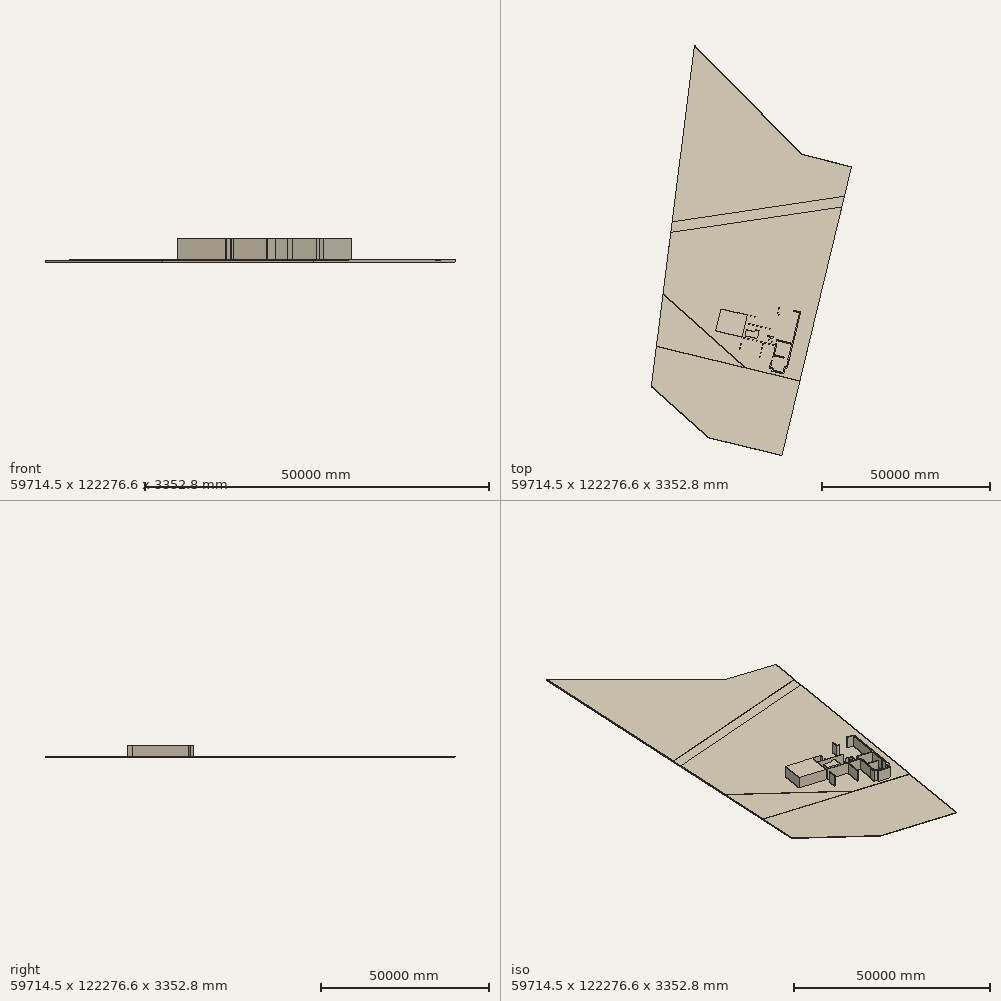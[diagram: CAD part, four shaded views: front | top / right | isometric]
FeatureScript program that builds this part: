
annotation { "Feature Type Name" : "Feature", "Feature Type Description" : "" }
export const myFeature = defineFeature(function(context is Context, id is Id, definition is map)
    precondition{}
    {
        {
            var Q0;
            Q0=qCreatedBy(makeId("Top.planeOp"),FACE);
            var sketch = newSketch(context, id + "F0", { "sketchPlane" : qUnion([Q0])});
            skLineSegment(sketch, "E0", {"start": v(0, 0) * mm, "end": v(31989.83, -32467.96) * mm});
            skLineSegment(sketch, "E1", {"start": v(31989.83, -32467.96) * mm, "end": v(46862.18, -36229.17) * mm});
            skLineSegment(sketch, "E2", {"start": v(46862.18, -36229.17) * mm, "end": v(26112.23, -122276.56) * mm});
            skLineSegment(sketch, "E3", {"start": v(46862.18, -36229.17) * mm, "end": v(46862.18, -51469.17) * mm, "construction": true});
            skLineSegment(sketch, "E4", {"start": v(0, 0) * mm, "end": v(-12852.3, -101676.89) * mm});
            skLineSegment(sketch, "E5", {"start": v(0, 0) * mm, "end": v(0, 15240) * mm, "construction": true});
            skLineSegment(sketch, "E6", {"start": v(26112.23, -122276.56) * mm, "end": v(4230, -116999.76) * mm});
            skLineSegment(sketch, "E7", {"start": v(26112.23, -122276.56) * mm, "end": v(10872.23, -122276.56) * mm, "construction": true});
            skLineSegment(sketch, "E8", {"start": v(4230, -116999.76) * mm, "end": v(-12852.3, -101676.89) * mm});
            skArc(sketch, "E9", {"start": v(-4165.07, -109469.35) * mm, "mid": v(-689.73, -114039.67) * mm, "end": v(4230, -116999.76) * mm, "construction": true});
            skArc(sketch, "E10", {"start": v(-4165.07, -109469.35) * mm, "mid": v(-8132.26, -105153.47) * mm, "end": v(-12852.3, -101676.89) * mm, "construction": true});
            skLineSegment(sketch, "E11", {"start": v(31471.2, -100053.58) * mm, "end": v(-11342.08, -89729.35) * mm});
            skLineSegment(sketch, "E12", {"start": v(-9365.85, -74095.03) * mm, "end": v(15198.72, -96129.54) * mm});
            skLineSegment(sketch, "E13", {"start": v(-6651.63, -52622.31) * mm, "end": v(44754.67, -44968.73) * mm});
            skLineSegment(sketch, "E14", {"start": v(-7048.63, -55763.02) * mm, "end": v(43983.88, -48165.09) * mm});
            skSolve(sketch);
        }
        {
            var Q0;
            {var subQ4=sQuery(id+"F0.wireOp",EDGE,"E0");Q0=makeQuery(id+"F0.imprint","IMPRINT",FACE,{"disambiguationData":[TD([[makeQuery(id+"F0.imprint","IMPRINT",EDGE,{"derivedFrom":subQ4}),-1.0]])]});}
            var Q1;
            {var subQ0=sQuery(id+"F0.wireOp",EDGE,"E13");Q1=makeQuery(id+"F0.imprint","IMPRINT",FACE,{"disambiguationData":[TD([[makeQuery(id+"F0.imprint","IMPRINT",EDGE,{"derivedFrom":subQ0}),-1.0]])]});}
            var Q2;
            {var subQ0=sQuery(id+"F0.wireOp",EDGE,"E12");Q2=makeQuery(id+"F0.imprint","IMPRINT",FACE,{"disambiguationData":[TD([[makeQuery(id+"F0.imprint","IMPRINT",EDGE,{"derivedFrom":subQ0}),1.0]])]});}
            var Q3;
            {var subQ3=sQuery(id+"F0.wireOp",EDGE,"E12");Q3=makeQuery(id+"F0.imprint","IMPRINT",FACE,{"disambiguationData":[TD([[makeQuery(id+"F0.imprint","IMPRINT",EDGE,{"derivedFrom":subQ3}),-1.0]])]});}
            var Q4;
            {var subQ1=sQuery(id+"F0.wireOp",EDGE,"E6");Q4=makeQuery(id+"F0.imprint","IMPRINT",FACE,{"disambiguationData":[TD([[makeQuery(id+"F0.imprint","IMPRINT",EDGE,{"derivedFrom":subQ1}),-1.0]])]});}
            extrude(context, id + "F1", {"entities" : qUnion([Q0, Q1, Q2, Q3, Q4]), "depth" : 304.8 * mm, "offsetDistance" : 25.4 * mm});
        }
        {
            var Q0;
            Q0=makeQuery(id+"F1.opExtrude","CAP_FACE",FACE,{"disambiguationData":[OSD([sQuery(id+"F0.wireOp",EDGE,"E0"),sQuery(id+"F0.wireOp",EDGE,"E1"),sQuery(id+"F0.wireOp",EDGE,"E2"),sQuery(id+"F0.wireOp",EDGE,"E4"),sQuery(id+"F0.wireOp",EDGE,"E6"),sQuery(id+"F0.wireOp",EDGE,"E8")])],"isStart":false});
            var sketch = newSketch(context, id + "F2", { "sketchPlane" : qUnion([Q0])});
            skLineSegment(sketch, "E15.0", {"start": v(-9365.85, -74095.03) * mm, "end": v(15198.72, -96129.54) * mm});
            skLineSegment(sketch, "E16.0", {"start": v(31471.2, -100053.58) * mm, "end": v(-11342.08, -89729.35) * mm});
            skLineSegment(sketch, "E17.0", {"start": v(0, 0) * mm, "end": v(-12852.3, -101676.89) * mm});
            skSolve(sketch);
        }
        {
            var Q0;
            {var subQ0=sQuery(id+"F2.wireOp",EDGE,"E15.0");Q0=makeQuery(id+"F2.imprint","IMPRINT",FACE,{"disambiguationData":[TD([[makeQuery(id+"F2.imprint","IMPRINT",EDGE,{"derivedFrom":subQ0}),-1.0]])]});}
            extrude(context, id + "F3", {"entities" : qUnion([Q0]), "operationType" : NewBodyOperationType.REMOVE, "oppositeDirection" : true, "depth" : 76.2 * mm, "offsetDistance" : 25.4 * mm});
        }
        {
            var Q0;
            Q0=makeQuery(id+"F1.opExtrude","CAP_FACE",FACE,{"disambiguationData":[OSD([sQuery(id+"F0.wireOp",EDGE,"E0"),sQuery(id+"F0.wireOp",EDGE,"E1"),sQuery(id+"F0.wireOp",EDGE,"E2"),sQuery(id+"F0.wireOp",EDGE,"E4"),sQuery(id+"F0.wireOp",EDGE,"E6"),sQuery(id+"F0.wireOp",EDGE,"E8")])],"isStart":false});
            var sketch = newSketch(context, id + "F4", { "sketchPlane" : qUnion([Q0])});
            skLineSegment(sketch, "E18.0", {"start": v(0, 0) * mm, "end": v(-12852.3, -101676.89) * mm});
            skLineSegment(sketch, "E19.0", {"start": v(4230, -116999.76) * mm, "end": v(-12852.3, -101676.89) * mm});
            skLineSegment(sketch, "E20.0", {"start": v(26112.23, -122276.56) * mm, "end": v(4230, -116999.76) * mm});
            skLineSegment(sketch, "E21.0", {"start": v(46862.18, -36229.17) * mm, "end": v(26112.23, -122276.56) * mm});
            skLineSegment(sketch, "E22.0", {"start": v(31471.2, -100053.58) * mm, "end": v(-11342.08, -89729.35) * mm});
            skSolve(sketch);
        }
        {
            var Q0;
            {var subQ4=sQuery(id+"F4.wireOp",EDGE,"E19.0");Q0=makeQuery(id+"F4.imprint","IMPRINT",FACE,{"disambiguationData":[TD([[makeQuery(id+"F4.imprint","IMPRINT",EDGE,{"derivedFrom":subQ4}),-1.0]])]});}
            extrude(context, id + "F5", {"entities" : qUnion([Q0]), "operationType" : NewBodyOperationType.REMOVE, "oppositeDirection" : true, "depth" : 152.4 * mm, "offsetDistance" : 25.4 * mm});
        }
        {
            var Q0;
            Q0=makeQuery(id+"F1.opExtrude","CAP_FACE",FACE,{"disambiguationData":[OSD([sQuery(id+"F0.wireOp",EDGE,"E0"),sQuery(id+"F0.wireOp",EDGE,"E1"),sQuery(id+"F0.wireOp",EDGE,"E2"),sQuery(id+"F0.wireOp",EDGE,"E4"),sQuery(id+"F0.wireOp",EDGE,"E6"),sQuery(id+"F0.wireOp",EDGE,"E8")])],"isStart":false});
            var sketch = newSketch(context, id + "F6", { "sketchPlane" : qUnion([Q0])});
            skLineSegment(sketch, "E23.0", {"start": v(-6651.63, -52622.31) * mm, "end": v(44754.67, -44968.73) * mm});
            skLineSegment(sketch, "E24.0", {"start": v(-7048.63, -55763.02) * mm, "end": v(43983.88, -48165.09) * mm});
            skLineSegment(sketch, "E25.0", {"start": v(0, 0) * mm, "end": v(-12852.3, -101676.89) * mm});
            skLineSegment(sketch, "E26.0", {"start": v(46862.18, -36229.17) * mm, "end": v(26112.23, -122276.56) * mm});
            skSolve(sketch);
        }
        {
            var Q0;
            {var subQ0=sQuery(id+"F6.wireOp",EDGE,"E23.0");Q0=makeQuery(id+"F6.imprint","IMPRINT",FACE,{"disambiguationData":[TD([[makeQuery(id+"F6.imprint","IMPRINT",EDGE,{"derivedFrom":subQ0}),-1.0]])]});}
            extrude(context, id + "F7", {"entities" : qUnion([Q0]), "operationType" : NewBodyOperationType.REMOVE, "oppositeDirection" : true, "depth" : 152.4 * mm, "offsetDistance" : 25.4 * mm});
        }
        {
            var Q0;
            {var subQ0=sQuery(id+"F0.wireOp",EDGE,"E4");var subQ1=sQuery(id+"F0.wireOp",EDGE,"E2");Q0=makeQuery(id+"F7.boolean.opBoolean","SPLIT",FACE,{"disambiguationData":[TD([makeQuery(id+"F3.boolean.opBoolean","COPY",FACE,{"derivedFrom":makeQuery(id+"F3.opExtrude","SWEPT_FACE",FACE,{"disambiguationData":[OSD([sQuery(id+"F2.wireOp",EDGE,"E15.0")])]})})])],"derivedFrom":makeQuery(id+"F1.opExtrude","CAP_FACE",FACE,{"disambiguationData":[OSD([sQuery(id+"F0.wireOp",EDGE,"E0"),sQuery(id+"F0.wireOp",EDGE,"E1"),subQ1,subQ0,sQuery(id+"F0.wireOp",EDGE,"E6"),sQuery(id+"F0.wireOp",EDGE,"E8")])],"isStart":false})});}
            var sketch = newSketch(context, id + "F8", { "sketchPlane" : qUnion([Q0])});
            skLineSegment(sketch, "E27", {"start": v(27669.68, -96315.03) * mm, "end": v(31724.64, -79499.64) * mm});
            skPoint(sketch, "E28.orphan", {"position": v(31471.2, -100053.58) * mm});
            skLineSegment(sketch, "E29", {"start": v(-5717.12, -79311.3) * mm, "end": v(3764.68, -81597.8) * mm});
            skLineSegment(sketch, "E30", {"start": v(3764.68, -81597.8) * mm, "end": v(7766.05, -65004.64) * mm});
            skLineSegment(sketch, "E31", {"start": v(7766.05, -65004.64) * mm, "end": v(-1715.76, -62718.14) * mm});
            skLineSegment(sketch, "E32", {"start": v(-1715.76, -62718.14) * mm, "end": v(-5717.12, -79311.3) * mm});
            skLineSegment(sketch, "E33", {"start": v(-5145.5, -76940.85) * mm, "end": v(-2182.44, -77655.38) * mm});
            skLineSegment(sketch, "E34", {"start": v(-2182.44, -77655.38) * mm, "end": v(-2754.06, -80025.83) * mm});
            skLineSegment(sketch, "E35", {"start": v(-5145.5, -76940.85) * mm, "end": v(-9590.1, -75869.05) * mm});
            skLineSegment(sketch, "E36", {"start": v(-2182.44, -77655.38) * mm, "end": v(1247.3, -63432.67) * mm});
            skLineSegment(sketch, "E37", {"start": v(3764.68, -81597.8) * mm, "end": v(7190.64, -82423.95) * mm});
            skLineSegment(sketch, "E38", {"start": v(4934.3, -91780.7) * mm, "end": v(-10343.91, -88096.42) * mm});
            skLineSegment(sketch, "E39.0", {"start": v(4230, -116999.76) * mm, "end": v(-12852.3, -101676.89) * mm});
            skLineSegment(sketch, "E40", {"start": v(-2047.33, -90097.1) * mm, "end": v(-6264.7, -107585.98) * mm});
            skLineSegment(sketch, "E41", {"start": v(-5603, -89239.67) * mm, "end": v(-9358.03, -104811.25) * mm});
            skArc(sketch, "E42", {"start": v(-6746.26, -93980.57) * mm, "mid": v(-7326.44, -90293.4) * mm, "end": v(-10343.91, -88096.42) * mm});
            skLineSegment(sketch, "E43", {"start": v(-8087.58, -78739.68) * mm, "end": v(-10343.91, -88096.42) * mm});
            skLineSegment(sketch, "E44", {"start": v(-5717.12, -79311.3) * mm, "end": v(-8087.58, -78739.68) * mm});
            skLineSegment(sketch, "E45", {"start": v(22775.38, -94507.71) * mm, "end": v(22346.66, -96285.55) * mm});
            skLineSegment(sketch, "E46", {"start": v(22346.66, -96285.55) * mm, "end": v(23235.58, -96499.91) * mm});
            skLineSegment(sketch, "E47", {"start": v(23235.58, -96499.91) * mm, "end": v(23092.67, -97092.52) * mm});
            skLineSegment(sketch, "E48", {"start": v(23092.67, -97092.52) * mm, "end": v(26648.35, -97949.96) * mm});
            skLineSegment(sketch, "E49", {"start": v(26648.35, -97949.96) * mm, "end": v(27077.07, -96172.12) * mm});
            skLineSegment(sketch, "E50", {"start": v(13071.34, -92167.63) * mm, "end": v(14241.39, -87315.61) * mm});
            skLineSegment(sketch, "E51", {"start": v(14241.39, -87315.61) * mm, "end": v(5985.04, -85324.63) * mm});
            skLineSegment(sketch, "E52", {"start": v(5985.04, -85324.63) * mm, "end": v(7699.91, -78213.28) * mm});
            skLineSegment(sketch, "E53", {"start": v(14020.33, -75230.32) * mm, "end": v(31724.64, -79499.64) * mm});
            skLineSegment(sketch, "E54.trimOffspring", {"start": v(27077.07, -96172.12) * mm, "end": v(27669.68, -96315.03) * mm});
            skLineSegment(sketch, "E55.0", {"start": v(6352.8, -85099.78) * mm, "end": v(7924.77, -78581.03) * mm});
            skLineSegment(sketch, "E55.1", {"start": v(23460.43, -96867.67) * mm, "end": v(26423.5, -97582.2) * mm});
            skLineSegment(sketch, "E55.2", {"start": v(26423.5, -97582.2) * mm, "end": v(26852.22, -95804.36) * mm});
            skLineSegment(sketch, "E55.3", {"start": v(26852.22, -95804.36) * mm, "end": v(27444.83, -95947.27) * mm});
            skLineSegment(sketch, "E55.4", {"start": v(27444.83, -95947.27) * mm, "end": v(28016.45, -93576.82) * mm});
            skLineSegment(sketch, "E55.5", {"start": v(23603.34, -96275.06) * mm, "end": v(23460.43, -96867.67) * mm});
            skLineSegment(sketch, "E55.6", {"start": v(14245.18, -75598.08) * mm, "end": v(19282.4, -76812.78) * mm});
            skLineSegment(sketch, "E55.7", {"start": v(22714.42, -96060.7) * mm, "end": v(23603.34, -96275.06) * mm});
            skLineSegment(sketch, "E55.8", {"start": v(23143.14, -94282.86) * mm, "end": v(22714.42, -96060.7) * mm});
            skLineSegment(sketch, "E55.9", {"start": v(13439.1, -91942.77) * mm, "end": v(23143.14, -94282.86) * mm});
            skLineSegment(sketch, "E55.10", {"start": v(13439.1, -91942.77) * mm, "end": v(14609.14, -87090.76) * mm});
            skLineSegment(sketch, "E55.11", {"start": v(14609.14, -87090.76) * mm, "end": v(6352.8, -85099.78) * mm});
            skLineSegment(sketch, "E56", {"start": v(14609.14, -87090.76) * mm, "end": v(19350.05, -88234) * mm});
            skLineSegment(sketch, "E57", {"start": v(20619.6, -88657.73) * mm, "end": v(19476.35, -93398.63) * mm});
            skLineSegment(sketch, "E58.0", {"start": v(20508.48, -88630.93) * mm, "end": v(19365.23, -93371.83) * mm});
            skLineSegment(sketch, "E58.1", {"start": v(14582.35, -87201.87) * mm, "end": v(20508.48, -88630.93) * mm});
            skLineSegment(sketch, "E59", {"start": v(17710.43, -83331.52) * mm, "end": v(18255.26, -81072.19) * mm});
            skLineSegment(sketch, "E60", {"start": v(17821.54, -83358.32) * mm, "end": v(18393.17, -80987.87) * mm});
            skLineSegment(sketch, "E61", {"start": v(7924.77, -78581.03) * mm, "end": v(18255.26, -81072.19) * mm});
            skLineSegment(sketch, "E62", {"start": v(14020.33, -75230.32) * mm, "end": v(12993.2, -79489.73) * mm});
            skLineSegment(sketch, "E63", {"start": v(12993.2, -79489.73) * mm, "end": v(7699.91, -78213.28) * mm});
            skLineSegment(sketch, "E64", {"start": v(14245.18, -75598.08) * mm, "end": v(13218.05, -79857.49) * mm});
            skLineSegment(sketch, "E65", {"start": v(13244.84, -79746.37) * mm, "end": v(18985.78, -81130.77) * mm});
            skLineSegment(sketch, "E66", {"start": v(23143.14, -94282.86) * mm, "end": v(23571.86, -92505.02) * mm});
            skLineSegment(sketch, "E67", {"start": v(24202.07, -89404.05) * mm, "end": v(19350.05, -88234) * mm});
            skLineSegment(sketch, "E68", {"start": v(23032.02, -94256.07) * mm, "end": v(24175.27, -89515.16) * mm});
            skLineSegment(sketch, "E69", {"start": v(24175.27, -89515.16) * mm, "end": v(20619.6, -88657.73) * mm});
            skLineSegment(sketch, "E70", {"start": v(19833.61, -91917.1) * mm, "end": v(21018.84, -92202.9) * mm});
            skLineSegment(sketch, "E71", {"start": v(21018.84, -92202.9) * mm, "end": v(21519, -90128.76) * mm});
            skLineSegment(sketch, "E72", {"start": v(21519, -90128.76) * mm, "end": v(23889.46, -90700.39) * mm});
            skLineSegment(sketch, "E73", {"start": v(23571.86, -92505.02) * mm, "end": v(28016.45, -93576.82) * mm});
            skLineSegment(sketch, "E74", {"start": v(23828.5, -92253.37) * mm, "end": v(27982.96, -93255.2) * mm});
            skLineSegment(sketch, "E75", {"start": v(28983.3, -89106.91) * mm, "end": v(24828.84, -88105.08) * mm});
            skLineSegment(sketch, "E76", {"start": v(27982.96, -93255.2) * mm, "end": v(28983.3, -89106.91) * mm});
            skLineSegment(sketch, "E77", {"start": v(23828.5, -92253.37) * mm, "end": v(24828.84, -88105.08) * mm});
            skLineSegment(sketch, "E78.trimOffspring", {"start": v(29159.7, -88835.91) * mm, "end": v(31356.88, -79724.5) * mm});
            skLineSegment(sketch, "E79", {"start": v(29159.7, -88835.91) * mm, "end": v(24603.99, -87737.32) * mm});
            skLineSegment(sketch, "E80", {"start": v(24603.99, -87737.32) * mm, "end": v(24202.07, -89404.05) * mm});
            skLineSegment(sketch, "E81", {"start": v(26023.36, -78438.34) * mm, "end": v(24951.57, -82882.93) * mm});
            skLineSegment(sketch, "E82", {"start": v(24951.57, -82882.93) * mm, "end": v(30285.09, -84169.09) * mm});
            skLineSegment(sketch, "E83", {"start": v(25912.25, -78411.54) * mm, "end": v(24340.28, -84930.28) * mm});
            skLineSegment(sketch, "E84", {"start": v(24924.77, -82994.05) * mm, "end": v(30258.3, -84280.2) * mm});
            skLineSegment(sketch, "E85", {"start": v(21057.5, -78390.48) * mm, "end": v(23724.26, -79033.55) * mm});
            skLineSegment(sketch, "E86", {"start": v(23724.26, -79033.55) * mm, "end": v(23474.18, -80070.63) * mm});
            skLineSegment(sketch, "E87", {"start": v(23474.18, -80070.63) * mm, "end": v(20807.42, -79427.55) * mm});
            skLineSegment(sketch, "E88", {"start": v(20807.42, -79427.55) * mm, "end": v(21057.5, -78390.48) * mm});
            skLineSegment(sketch, "E89", {"start": v(12993.2, -79489.73) * mm, "end": v(12921.74, -79786.03) * mm});
            skLineSegment(sketch, "E90", {"start": v(17821.54, -83358.32) * mm, "end": v(24340.28, -84930.28) * mm});
            skLineSegment(sketch, "E91", {"start": v(25961.85, -83244.13) * mm, "end": v(25553.97, -84935.55) * mm});
            skLineSegment(sketch, "E92", {"start": v(15313.18, -82871.01) * mm, "end": v(24424.6, -85068.2) * mm});
            skLineSegment(sketch, "E93", {"start": v(24424.6, -85068.2) * mm, "end": v(24924.77, -82994.05) * mm});
            skLineSegment(sketch, "E94", {"start": v(25054.81, -81967.22) * mm, "end": v(24462.2, -81824.31) * mm});
            skLineSegment(sketch, "E95", {"start": v(24462.2, -81824.31) * mm, "end": v(23747.67, -84787.38) * mm});
            skLineSegment(sketch, "E96", {"start": v(22853.5, -83944.68) * mm, "end": v(17964.45, -82765.7) * mm});
            skLineSegment(sketch, "E97", {"start": v(18807.15, -81871.54) * mm, "end": v(19343.04, -79649.24) * mm});
            skLineSegment(sketch, "E98", {"start": v(20165.76, -80788.24) * mm, "end": v(19879.94, -81973.47) * mm});
            skLineSegment(sketch, "E99", {"start": v(19879.94, -81973.47) * mm, "end": v(23139.32, -82759.45) * mm});
            skLineSegment(sketch, "E100", {"start": v(23139.32, -82759.45) * mm, "end": v(23425.13, -81574.23) * mm});
            skLineSegment(sketch, "E101", {"start": v(23425.13, -81574.23) * mm, "end": v(20165.76, -80788.24) * mm});
            skLineSegment(sketch, "E102", {"start": v(19282.4, -76812.78) * mm, "end": v(25912.25, -78411.54) * mm});
            skLineSegment(sketch, "E103.trimOffspring", {"start": v(26023.36, -78438.34) * mm, "end": v(31356.88, -79724.5) * mm});
            skLineSegment(sketch, "E104", {"start": v(27837.43, -93533.65) * mm, "end": v(27908.89, -93237.34) * mm});
            skLineSegment(sketch, "E105", {"start": v(26948.51, -93319.29) * mm, "end": v(27019.97, -93022.98) * mm});
            skLineSegment(sketch, "E106", {"start": v(26972.33, -93220.52) * mm, "end": v(27861.25, -93434.88) * mm});
            skLineSegment(sketch, "E107", {"start": v(26963.4, -93257.56) * mm, "end": v(27852.32, -93471.92) * mm});
            skLineSegment(sketch, "E108", {"start": v(24810.98, -88179.16) * mm, "end": v(24514.67, -88107.7) * mm});
            skLineSegment(sketch, "E109", {"start": v(24300.31, -88996.63) * mm, "end": v(24596.62, -89068.08) * mm});
            skLineSegment(sketch, "E110", {"start": v(24362.04, -89011.51) * mm, "end": v(24576.4, -88122.6) * mm});
            skLineSegment(sketch, "E111", {"start": v(24399.08, -89020.44) * mm, "end": v(24613.44, -88131.52) * mm});
            skLineSegment(sketch, "E112", {"start": v(23016.84, -89118.24) * mm, "end": v(23543.8, -86932.98) * mm});
            skLineSegment(sketch, "E113", {"start": v(22905.73, -89091.44) * mm, "end": v(23405.9, -87017.3) * mm});
            skLineSegment(sketch, "E114", {"start": v(15884.8, -80500.56) * mm, "end": v(14312.84, -87019.3) * mm});
            skLineSegment(sketch, "E115", {"start": v(15339.97, -82759.9) * mm, "end": v(17710.43, -83331.52) * mm});
            skLineSegment(sketch, "E116", {"start": v(18807.15, -81871.54) * mm, "end": v(18214.53, -81728.63) * mm});
            skLineSegment(sketch, "E117", {"start": v(13071.34, -92167.63) * mm, "end": v(23071.68, -94579.17) * mm});
            skLineSegment(sketch, "E118", {"start": v(19247.36, -85896.9) * mm, "end": v(23543.8, -86932.98) * mm});
            skLineSegment(sketch, "E119", {"start": v(19109.45, -85981.23) * mm, "end": v(19739.1, -86133.06) * mm});
            skLineSegment(sketch, "E120", {"start": v(22016.8, -88877.08) * mm, "end": v(22516.98, -86802.94) * mm});
            skLineSegment(sketch, "E121", {"start": v(21905.7, -88850.29) * mm, "end": v(22405.86, -86776.14) * mm});
            skLineSegment(sketch, "E122", {"start": v(20090.81, -88412.64) * mm, "end": v(20590.98, -86338.5) * mm});
            skLineSegment(sketch, "E123", {"start": v(20201.93, -88439.43) * mm, "end": v(20702.1, -86365.29) * mm});
            skLineSegment(sketch, "E124", {"start": v(20344.83, -87846.82) * mm, "end": v(22048.6, -88257.67) * mm});
            skCircle(sketch, "E125", {"center": v(20717.84, -88250.3) * mm, "radius": 152.4 * mm});
            skCircle(sketch, "E126", {"center": v(21532.68, -88446.8) * mm, "radius": 152.4 * mm});
            skLineSegment(sketch, "E127", {"start": v(19473.5, -88263.78) * mm, "end": v(19544.96, -87967.47) * mm});
            skLineSegment(sketch, "E128", {"start": v(19544.96, -87967.47) * mm, "end": v(20038.8, -88086.56) * mm});
            skLineSegment(sketch, "E129", {"start": v(20038.8, -88086.56) * mm, "end": v(19967.35, -88382.87) * mm});
            skLineSegment(sketch, "E130", {"start": v(19643.73, -87991.29) * mm, "end": v(19756.86, -87522.14) * mm});
            skLineSegment(sketch, "E131", {"start": v(19756.86, -87522.14) * mm, "end": v(20053.17, -87593.59) * mm});
            skLineSegment(sketch, "E132", {"start": v(20053.17, -87593.59) * mm, "end": v(19940.04, -88062.74) * mm});
            skLineSegment(sketch, "E133", {"start": v(19760.9, -86530.24) * mm, "end": v(20501.67, -86708.88) * mm});
            skLineSegment(sketch, "E134", {"start": v(20600.87, -86785.05) * mm, "end": v(20489.76, -86758.26) * mm});
            skLineSegment(sketch, "E135", {"start": v(20346.85, -87350.87) * mm, "end": v(20457.97, -87377.67) * mm});
            skLineSegment(sketch, "E136", {"start": v(20402.41, -87364.27) * mm, "end": v(20545.32, -86771.66) * mm});
            skArc(sketch, "E137", {"start": v(20402.41, -87364.27) * mm, "mid": v(20012.42, -87067.68) * mm, "end": v(19966.67, -86579.86) * mm, "construction": true});
            skLineSegment(sketch, "E138", {"start": v(22231.16, -87988.16) * mm, "end": v(23120.08, -88202.52) * mm});
            skLineSegment(sketch, "E139", {"start": v(23120.08, -88202.52) * mm, "end": v(22016.8, -88877.08) * mm});
            skLineSegment(sketch, "E140", {"start": v(22231.16, -87988.16) * mm, "end": v(22905.73, -89091.44) * mm});
            skCircle(sketch, "E141", {"center": v(22568.44, -88539.8) * mm, "radius": 50.8 * mm});
            skLineSegment(sketch, "E142", {"start": v(22427.66, -87173.32) * mm, "end": v(23316.58, -87387.68) * mm});
            skLineSegment(sketch, "E143", {"start": v(22304.64, -87195.9) * mm, "end": v(22415.75, -87222.7) * mm});
            skLineSegment(sketch, "E144", {"start": v(22161.73, -87788.52) * mm, "end": v(22272.85, -87815.32) * mm});
            skLineSegment(sketch, "E145", {"start": v(22360.2, -87209.3) * mm, "end": v(22217.29, -87801.92) * mm});
            skArc(sketch, "E146", {"start": v(22217.29, -87801.92) * mm, "mid": v(22699.6, -87715.68) * mm, "end": v(22962.65, -87302.33) * mm, "construction": true});
            skLineSegment(sketch, "E147", {"start": v(19461.72, -85007.99) * mm, "end": v(21239.56, -85436.7) * mm});
            skLineSegment(sketch, "E148", {"start": v(19390.27, -85304.3) * mm, "end": v(21168.1, -85733.01) * mm});
            skLineSegment(sketch, "E149", {"start": v(20612.78, -86735.67) * mm, "end": v(20909.09, -86807.12) * mm});
            skLineSegment(sketch, "E150", {"start": v(21239.56, -85436.7) * mm, "end": v(21025.2, -86325.63) * mm});
            skLineSegment(sketch, "E151", {"start": v(21980.33, -85615.34) * mm, "end": v(21765.97, -86504.26) * mm});
            skLineSegment(sketch, "E152", {"start": v(21099.28, -86343.49) * mm, "end": v(21072.48, -86454.6) * mm});
            skLineSegment(sketch, "E153", {"start": v(21691.9, -86486.4) * mm, "end": v(21665.1, -86597.5) * mm});
            skLineSegment(sketch, "E154", {"start": v(21085.88, -86399.05) * mm, "end": v(21678.5, -86541.95) * mm});
            skLineSegment(sketch, "E155", {"start": v(20909.09, -86807.12) * mm, "end": v(20998.4, -86436.74) * mm});
            skLineSegment(sketch, "E156", {"start": v(21649.86, -86985.76) * mm, "end": v(21739.17, -86615.37) * mm});
            skLineSegment(sketch, "E157.trimOffspring", {"start": v(21649.86, -86985.76) * mm, "end": v(22316.55, -87146.52) * mm});
            skLineSegment(sketch, "E158.trimOffspring", {"start": v(21908.87, -85911.64) * mm, "end": v(23686.71, -86340.36) * mm});
            skLineSegment(sketch, "E159.trimOffspring", {"start": v(21980.33, -85615.34) * mm, "end": v(23758.16, -86044.06) * mm});
            skLineSegment(sketch, "E160", {"start": v(15482.88, -82167.29) * mm, "end": v(17853.33, -82738.9) * mm});
            skLineSegment(sketch, "E161", {"start": v(15741.9, -81093.17) * mm, "end": v(18112.35, -81664.8) * mm});
            skLineSegment(sketch, "E162", {"start": v(17889.06, -82590.76) * mm, "end": v(18000.17, -82617.55) * mm});
            skLineSegment(sketch, "E163", {"start": v(18067.7, -81850) * mm, "end": v(18178.8, -81876.79) * mm});
            skLineSegment(sketch, "E164", {"start": v(18123.25, -81863.39) * mm, "end": v(17944.62, -82604.15) * mm});
            skLineSegment(sketch, "E165", {"start": v(15397.07, -82035.55) * mm, "end": v(15508.19, -82062.34) * mm});
            skLineSegment(sketch, "E166", {"start": v(15611.43, -81146.63) * mm, "end": v(15722.55, -81173.42) * mm});
            skLineSegment(sketch, "E167", {"start": v(15666.99, -81160.03) * mm, "end": v(15452.63, -82048.95) * mm});
            skLineSegment(sketch, "E168", {"start": v(22853.5, -83944.68) * mm, "end": v(22710.6, -84537.3) * mm});
            skLineSegment(sketch, "E169", {"start": v(22784.67, -84555.16) * mm, "end": v(22757.88, -84666.27) * mm});
            skLineSegment(sketch, "E170", {"start": v(23673.6, -84769.51) * mm, "end": v(23646.8, -84880.63) * mm});
            skLineSegment(sketch, "E171", {"start": v(25412.08, -80485.69) * mm, "end": v(24708.35, -80315.99) * mm});
            skLineSegment(sketch, "E172", {"start": v(24708.35, -80315.99) * mm, "end": v(25208.52, -78241.84) * mm});
            skLineSegment(sketch, "E173", {"start": v(25319.64, -78268.64) * mm, "end": v(24846.26, -80231.67) * mm});
            skLineSegment(sketch, "E174", {"start": v(24846.26, -80231.67) * mm, "end": v(25438.87, -80374.57) * mm});
            skLineSegment(sketch, "E175", {"start": v(26072.96, -83270.93) * mm, "end": v(25665.08, -84962.34) * mm});
            skLineSegment(sketch, "E176", {"start": v(25715.7, -84752.46) * mm, "end": v(29901.03, -85761.73) * mm});
            skLineSegment(sketch, "E177", {"start": v(25688.9, -84863.58) * mm, "end": v(29874.23, -85872.85) * mm});
            skLineSegment(sketch, "E178", {"start": v(28554.53, -83869.35) * mm, "end": v(28197.26, -85350.88) * mm});
            skLineSegment(sketch, "E179", {"start": v(28443.41, -83842.55) * mm, "end": v(28086.15, -85324.08) * mm});
            skLineSegment(sketch, "E180", {"start": v(27702.65, -83663.92) * mm, "end": v(27345.38, -85145.45) * mm});
            skLineSegment(sketch, "E181", {"start": v(25941.96, -83814.16) * mm, "end": v(26830.88, -84028.52) * mm});
            skLineSegment(sketch, "E182", {"start": v(26830.88, -84028.52) * mm, "end": v(26961.88, -83485.29) * mm});
            skLineSegment(sketch, "E183", {"start": v(27085.34, -83515.06) * mm, "end": v(27013.89, -83811.37) * mm});
            skLineSegment(sketch, "E184", {"start": v(27013.89, -83811.37) * mm, "end": v(27507.73, -83930.45) * mm});
            skLineSegment(sketch, "E185", {"start": v(27507.73, -83930.45) * mm, "end": v(27579.19, -83634.15) * mm});
            skLineSegment(sketch, "E186", {"start": v(27112.66, -83835.18) * mm, "end": v(26999.52, -84304.34) * mm});
            skLineSegment(sketch, "E187", {"start": v(26999.52, -84304.34) * mm, "end": v(27295.83, -84375.79) * mm});
            skLineSegment(sketch, "E188", {"start": v(27295.83, -84375.79) * mm, "end": v(27408.96, -83906.64) * mm});
            skLineSegment(sketch, "E189", {"start": v(25762.98, -84881.44) * mm, "end": v(25789.77, -84770.32) * mm});
            skLineSegment(sketch, "E190", {"start": v(26355.6, -85024.34) * mm, "end": v(26382.39, -84913.23) * mm});
            skLineSegment(sketch, "E191", {"start": v(25776.38, -84825.88) * mm, "end": v(26368.99, -84968.79) * mm});
            skArc(sketch, "E192", {"start": v(26368.99, -84968.79) * mm, "mid": v(26275.53, -84475.95) * mm, "end": v(25844.08, -84220.05) * mm, "construction": true});
            skLineSegment(sketch, "E193", {"start": v(28340.17, -84758.27) * mm, "end": v(30043.93, -85169.12) * mm});
            skLineSegment(sketch, "E194", {"start": v(28366.96, -84647.15) * mm, "end": v(30070.73, -85058) * mm});
            skLineSegment(sketch, "E195", {"start": v(29278.79, -88342.07) * mm, "end": v(27303.41, -87865.72) * mm});
            skLineSegment(sketch, "E196", {"start": v(27303.41, -87865.72) * mm, "end": v(27755.95, -85989.1) * mm});
            skLineSegment(sketch, "E197", {"start": v(27755.95, -85989.1) * mm, "end": v(29731.32, -86465.46) * mm});
            skLineSegment(sketch, "E198", {"start": v(28296.03, -85374.7) * mm, "end": v(28269.24, -85485.81) * mm});
            skLineSegment(sketch, "E199", {"start": v(29777.56, -85731.96) * mm, "end": v(29750.77, -85843.08) * mm});
            skLineSegment(sketch, "E200", {"start": v(29036.8, -85553.33) * mm, "end": v(29010, -85664.44) * mm});
            skLineSegment(sketch, "E201", {"start": v(28282.63, -85430.25) * mm, "end": v(29023.4, -85608.89) * mm});
            skLineSegment(sketch, "E202", {"start": v(29023.4, -85608.89) * mm, "end": v(29764.17, -85787.52) * mm});
            skArc(sketch, "E203", {"start": v(25137.16, -86664) * mm, "mid": v(24733.67, -87037.01) * mm, "end": v(24922.8, -87552.92) * mm});
            skLineSegment(sketch, "E204", {"start": v(26429.67, -85042.2) * mm, "end": v(26197.45, -86005.2) * mm});
            skLineSegment(sketch, "E205", {"start": v(26197.45, -86005.2) * mm, "end": v(25456.68, -85826.57) * mm});
            skLineSegment(sketch, "E206", {"start": v(26540.78, -85069) * mm, "end": v(26281.77, -86143.11) * mm});
            skLineSegment(sketch, "E207", {"start": v(26281.77, -86143.11) * mm, "end": v(25429.88, -85937.69) * mm});
            skLineSegment(sketch, "E208", {"start": v(26405.85, -85140.98) * mm, "end": v(26516.97, -85167.77) * mm});
            skLineSegment(sketch, "E209", {"start": v(26215.3, -85931.13) * mm, "end": v(26326.42, -85957.92) * mm});
            skLineSegment(sketch, "E210", {"start": v(26461.4, -85154.37) * mm, "end": v(26270.87, -85944.52) * mm});
            skArc(sketch, "E211", {"start": v(26270.87, -85944.52) * mm, "mid": v(26927.99, -85819.92) * mm, "end": v(27269.18, -85244.65) * mm, "construction": true});
            skLineSegment(sketch, "E212", {"start": v(25363.43, -85725.7) * mm, "end": v(25474.54, -85752.5) * mm});
            skLineSegment(sketch, "E213", {"start": v(25553.97, -84935.55) * mm, "end": v(25665.08, -84962.34) * mm});
            skLineSegment(sketch, "E214.trimOffspring", {"start": v(25363.43, -85725.7) * mm, "end": v(24863.26, -87799.85) * mm});
            skLineSegment(sketch, "E215.trimOffspring", {"start": v(25474.54, -85752.5) * mm, "end": v(24974.37, -87826.64) * mm});
            skLineSegment(sketch, "E216", {"start": v(24733.67, -87037.01) * mm, "end": v(25029.98, -87108.46) * mm, "construction": true});
            skLineSegment(sketch, "E217", {"start": v(23543.8, -86932.98) * mm, "end": v(23758.16, -86044.06) * mm});
            skLineSegment(sketch, "E218", {"start": v(20717.84, -88250.3) * mm, "end": v(21532.68, -88446.8) * mm, "construction": true});
            skLineSegment(sketch, "E219", {"start": v(14201.72, -86992.5) * mm, "end": v(15773.69, -80473.77) * mm});
            skLineSegment(sketch, "E220", {"start": v(15063.1, -83908.09) * mm, "end": v(19470.65, -84970.95) * mm});
            skLineSegment(sketch, "E221", {"start": v(19739.1, -86133.06) * mm, "end": v(19238.93, -88207.2) * mm});
            skLineSegment(sketch, "E222", {"start": v(19470.65, -84970.95) * mm, "end": v(19247.36, -85896.9) * mm});
            skLineSegment(sketch, "E223.trimOffspring", {"start": v(19850.22, -86159.86) * mm, "end": v(19350.05, -88234) * mm});
            skLineSegment(sketch, "E224.trimOffspring", {"start": v(19850.22, -86159.86) * mm, "end": v(23405.9, -87017.3) * mm});
            skLineSegment(sketch, "E225", {"start": v(15036.3, -84019.2) * mm, "end": v(19332.74, -85055.27) * mm});
            skLineSegment(sketch, "E226", {"start": v(19332.74, -85055.27) * mm, "end": v(19109.45, -85981.23) * mm});
            skLineSegment(sketch, "E227", {"start": v(23000.54, -90486.03) * mm, "end": v(23286.35, -89300.8) * mm});
            skLineSegment(sketch, "E228", {"start": v(20809.72, -93720.17) * mm, "end": v(20738.27, -94016.47) * mm});
            skLineSegment(sketch, "E229", {"start": v(21698.64, -93934.53) * mm, "end": v(21627.2, -94230.83) * mm});
            skLineSegment(sketch, "E230", {"start": v(20774, -93868.32) * mm, "end": v(21662.92, -94082.68) * mm});
            skLineSegment(sketch, "E231", {"start": v(18295.67, -84805.18) * mm, "end": v(18152.76, -85397.8) * mm});
            skLineSegment(sketch, "E232", {"start": v(18152.76, -85397.8) * mm, "end": v(15486, -84754.72) * mm});
            skLineSegment(sketch, "E233", {"start": v(15486, -84754.72) * mm, "end": v(15048.36, -86569.6) * mm});
            skLineSegment(sketch, "E234", {"start": v(15048.36, -86569.6) * mm, "end": v(18789.23, -87471.7) * mm});
            skLineSegment(sketch, "E235", {"start": v(18789.23, -87471.7) * mm, "end": v(19146.5, -85990.16) * mm});
            skLineSegment(sketch, "E236", {"start": v(18396.54, -84711.93) * mm, "end": v(18369.75, -84823.05) * mm});
            skLineSegment(sketch, "E237", {"start": v(19285.46, -84926.3) * mm, "end": v(19258.67, -85037.4) * mm});
            skLineSegment(sketch, "E238", {"start": v(18383.14, -84767.49) * mm, "end": v(19272.06, -84981.85) * mm});
            skArc(sketch, "E239", {"start": v(18383.14, -84767.49) * mm, "mid": v(18512.5, -85490.95) * mm, "end": v(19132.53, -85885.54) * mm, "construction": true});
            skArc(sketch, "E240", {"start": v(24399.08, -89020.44) * mm, "mid": v(25122.55, -88891.09) * mm, "end": v(25517.13, -88271.06) * mm, "construction": true});
            skArc(sketch, "E241", {"start": v(26972.33, -93220.52) * mm, "mid": v(27417.21, -92635.53) * mm, "end": v(28148.94, -92566.91) * mm, "construction": true});
            skArc(sketch, "E242", {"start": v(21678.5, -86541.95) * mm, "mid": v(21370.68, -86938.03) * mm, "end": v(20870.02, -86969.15) * mm, "construction": true});
            skLineSegment(sketch, "E243", {"start": v(28435.5, -91378.6) * mm, "end": v(27052.74, -91045.15) * mm});
            skLineSegment(sketch, "E244", {"start": v(26412.84, -90773.26) * mm, "end": v(25933.51, -92760.99) * mm});
            skLineSegment(sketch, "E245", {"start": v(25822.4, -92734.2) * mm, "end": v(26301.73, -90746.47) * mm});
            skLineSegment(sketch, "E246", {"start": v(27079.53, -90934.03) * mm, "end": v(28462.3, -91267.48) * mm});
            skLineSegment(sketch, "E247", {"start": v(27872.16, -88838.96) * mm, "end": v(27401.76, -90789.65) * mm});
            skLineSegment(sketch, "E248", {"start": v(27401.76, -90789.65) * mm, "end": v(28512.9, -91057.6) * mm});
            skLineSegment(sketch, "E249", {"start": v(27694.73, -91199.96) * mm, "end": v(27444.65, -92237.04) * mm});
            skLineSegment(sketch, "E250", {"start": v(27444.65, -92237.04) * mm, "end": v(27987.88, -92368.03) * mm});
            skLineSegment(sketch, "E251", {"start": v(27987.88, -92368.03) * mm, "end": v(28237.96, -91330.96) * mm});
            skLineSegment(sketch, "E252", {"start": v(27798.08, -88821.1) * mm, "end": v(27530.13, -89932.25) * mm});
            skLineSegment(sketch, "E253", {"start": v(27530.13, -89932.25) * mm, "end": v(25579.45, -89461.85) * mm});
            skLineSegment(sketch, "E254", {"start": v(25579.45, -89461.85) * mm, "end": v(25847.4, -88350.7) * mm});
            skLineSegment(sketch, "E255", {"start": v(27497.2, -91152.33) * mm, "end": v(27306.65, -91942.48) * mm});
            skLineSegment(sketch, "E256", {"start": v(27306.65, -91942.48) * mm, "end": v(26936.27, -91853.16) * mm});
            skLineSegment(sketch, "E257", {"start": v(26936.27, -91853.16) * mm, "end": v(27126.81, -91063.01) * mm});
            skLineSegment(sketch, "E258", {"start": v(24281.04, -90376.77) * mm, "end": v(26256.41, -90853.12) * mm});
            skLineSegment(sketch, "E259", {"start": v(26256.41, -90853.12) * mm, "end": v(25803.88, -92729.73) * mm});
            skLineSegment(sketch, "E260", {"start": v(27079.53, -90934.03) * mm, "end": v(27052.74, -91045.15) * mm});
            skLineSegment(sketch, "E261", {"start": v(26301.73, -90746.47) * mm, "end": v(26412.84, -90773.26) * mm});
            skLineSegment(sketch, "E262", {"start": v(13369.06, -90933.02) * mm, "end": v(13665.37, -91004.47) * mm});
            skLineSegment(sketch, "E263", {"start": v(14012.14, -88266.26) * mm, "end": v(14308.45, -88337.71) * mm});
            skLineSegment(sketch, "E264", {"start": v(14160.3, -88301.99) * mm, "end": v(13517.22, -90968.74) * mm});
            skLineSegment(sketch, "E265", {"start": v(30171.65, -79438.68) * mm, "end": v(31071.07, -80909.72) * mm});
            skLineSegment(sketch, "E266", {"start": v(30928.16, -81502.33) * mm, "end": v(30236.78, -81335.6) * mm});
            skLineSegment(sketch, "E267", {"start": v(30236.78, -81335.6) * mm, "end": v(29879.52, -82817.14) * mm});
            skLineSegment(sketch, "E268", {"start": v(29879.52, -82817.14) * mm, "end": v(30570.9, -82983.86) * mm});
            skLineSegment(sketch, "E269", {"start": v(25090.54, -81819.07) * mm, "end": v(25201.65, -81845.86) * mm});
            skLineSegment(sketch, "E270", {"start": v(25376.35, -80633.84) * mm, "end": v(25487.47, -80660.63) * mm});
            skLineSegment(sketch, "E271", {"start": v(24998.85, -83011.91) * mm, "end": v(25025.65, -82900.8) * mm});
            skLineSegment(sketch, "E272", {"start": v(25887.77, -83226.27) * mm, "end": v(25914.57, -83115.16) * mm});
            skLineSegment(sketch, "E273", {"start": v(25012.25, -82956.35) * mm, "end": v(25901.17, -83170.71) * mm});
            skArc(sketch, "E274", {"start": v(25901.17, -83170.71) * mm, "mid": v(25771.81, -82447.25) * mm, "end": v(25151.79, -82052.66) * mm, "construction": true});
            skLineSegment(sketch, "E275", {"start": v(28653.3, -83893.16) * mm, "end": v(28680.1, -83782.05) * mm});
            skLineSegment(sketch, "E276", {"start": v(29420.86, -83960.68) * mm, "end": v(29394.06, -84071.8) * mm});
            skLineSegment(sketch, "E277", {"start": v(30161.62, -84139.31) * mm, "end": v(30134.83, -84250.43) * mm});
            skLineSegment(sketch, "E278", {"start": v(28666.7, -83837.6) * mm, "end": v(29407.46, -84016.24) * mm});
            skLineSegment(sketch, "E279", {"start": v(29407.46, -84016.24) * mm, "end": v(30148.23, -84194.87) * mm});
            skLineSegment(sketch, "E280", {"start": v(26761.5, -78302.8) * mm, "end": v(26690.05, -78599.1) * mm});
            skLineSegment(sketch, "E281", {"start": v(27502.27, -78481.43) * mm, "end": v(27430.82, -78777.74) * mm});
            skLineSegment(sketch, "E282", {"start": v(27798.58, -78552.88) * mm, "end": v(27727.13, -78849.2) * mm});
            skLineSegment(sketch, "E283", {"start": v(28539.35, -78731.52) * mm, "end": v(28467.9, -79027.82) * mm});
            skLineSegment(sketch, "E284", {"start": v(28835.65, -78802.97) * mm, "end": v(28764.2, -79099.28) * mm});
            skLineSegment(sketch, "E285", {"start": v(29576.42, -78981.6) * mm, "end": v(29504.96, -79277.9) * mm});
            skLineSegment(sketch, "E286", {"start": v(27466.55, -78629.58) * mm, "end": v(26725.78, -78450.95) * mm});
            skLineSegment(sketch, "E287", {"start": v(27762.85, -78701.04) * mm, "end": v(28503.62, -78879.67) * mm});
            skLineSegment(sketch, "E288", {"start": v(28799.93, -78951.12) * mm, "end": v(29540.7, -79129.76) * mm});
            skLineSegment(sketch, "E289", {"start": v(26511.22, -82266.17) * mm, "end": v(26296.86, -83155.09) * mm});
            skLineSegment(sketch, "E290", {"start": v(26296.86, -83155.09) * mm, "end": v(28222.85, -83619.53) * mm});
            skLineSegment(sketch, "E291", {"start": v(28222.85, -83619.53) * mm, "end": v(28437.2, -82730.61) * mm});
            skLineSegment(sketch, "E292", {"start": v(28437.2, -82730.61) * mm, "end": v(26511.22, -82266.17) * mm});
            skLineSegment(sketch, "E293", {"start": v(27492.99, -78844.99) * mm, "end": v(29418.98, -79309.43) * mm});
            skLineSegment(sketch, "E294", {"start": v(29418.98, -79309.43) * mm, "end": v(29204.62, -80198.35) * mm});
            skLineSegment(sketch, "E295", {"start": v(29204.62, -80198.35) * mm, "end": v(27278.63, -79733.9) * mm});
            skLineSegment(sketch, "E296", {"start": v(27278.63, -79733.9) * mm, "end": v(27492.99, -78844.99) * mm});
            skLineSegment(sketch, "E297", {"start": v(25456.74, -80300.5) * mm, "end": v(25567.85, -80327.29) * mm});
            skLineSegment(sketch, "E298", {"start": v(25671.1, -79411.58) * mm, "end": v(25782.21, -79438.37) * mm});
            skLineSegment(sketch, "E299", {"start": v(25885.45, -78522.66) * mm, "end": v(25996.57, -78549.45) * mm});
            skLineSegment(sketch, "E300", {"start": v(25941.01, -78536.05) * mm, "end": v(25726.65, -79424.97) * mm});
            skLineSegment(sketch, "E301", {"start": v(25726.65, -79424.97) * mm, "end": v(25512.3, -80313.9) * mm});
            skLineSegment(sketch, "E302", {"start": v(14126.1, -76091.92) * mm, "end": v(14373.02, -76151.47) * mm});
            skLineSegment(sketch, "E303", {"start": v(14373.02, -76151.47) * mm, "end": v(13610.85, -79312.07) * mm});
            skLineSegment(sketch, "E304", {"start": v(13610.85, -79312.07) * mm, "end": v(13363.93, -79252.53) * mm});
            skLineSegment(sketch, "E305", {"start": v(13991.93, -77731.77) * mm, "end": v(13745.01, -77672.23) * mm});
            skLineSegment(sketch, "E306", {"start": v(13801.4, -78521.92) * mm, "end": v(13554.47, -78462.38) * mm});
            skLineSegment(sketch, "E307", {"start": v(14182.48, -76941.62) * mm, "end": v(13935.55, -76882.07) * mm});
            skLineSegment(sketch, "E308", {"start": v(14985.95, -75776.71) * mm, "end": v(14825.18, -76443.4) * mm});
            skLineSegment(sketch, "E309", {"start": v(14825.18, -76443.4) * mm, "end": v(18380.86, -77300.84) * mm});
            skLineSegment(sketch, "E310", {"start": v(17195.63, -77015.03) * mm, "end": v(17356.4, -76348.34) * mm});
            skLineSegment(sketch, "E311", {"start": v(16010.4, -76729.21) * mm, "end": v(16171.17, -76062.52) * mm});
            skLineSegment(sketch, "E312", {"start": v(18380.86, -77300.84) * mm, "end": v(18541.63, -76634.15) * mm});
            skLineSegment(sketch, "E313", {"start": v(14133.76, -79960.73) * mm, "end": v(14294.53, -79294.04) * mm});
            skLineSegment(sketch, "E314", {"start": v(14294.53, -79294.04) * mm, "end": v(17850.2, -80151.48) * mm});
            skLineSegment(sketch, "E315", {"start": v(17850.2, -80151.48) * mm, "end": v(17689.44, -80818.17) * mm});
            skLineSegment(sketch, "E316", {"start": v(15479.76, -79579.85) * mm, "end": v(15318.99, -80246.54) * mm});
            skLineSegment(sketch, "E317", {"start": v(16664.98, -79865.66) * mm, "end": v(16504.21, -80532.35) * mm});
            skLineSegment(sketch, "E318", {"start": v(17850.2, -80151.48) * mm, "end": v(18046.7, -79336.63) * mm});
            skLineSegment(sketch, "E319", {"start": v(18046.7, -79336.63) * mm, "end": v(19343.04, -79649.24) * mm});
            skLineSegment(sketch, "E320", {"start": v(19046.74, -79577.79) * mm, "end": v(18689.47, -81059.32) * mm});
            skLineSegment(sketch, "E321", {"start": v(18131.02, -79474.54) * mm, "end": v(18908.83, -79662.1) * mm});
            skLineSegment(sketch, "E322", {"start": v(18908.83, -79662.1) * mm, "end": v(18605.15, -80921.4) * mm});
            skLineSegment(sketch, "E323", {"start": v(18605.15, -80921.4) * mm, "end": v(17827.35, -80733.84) * mm});
            skLineSegment(sketch, "E324", {"start": v(17827.35, -80733.84) * mm, "end": v(18131.02, -79474.54) * mm});
            skLineSegment(sketch, "E325", {"start": v(19892.16, -77534.64) * mm, "end": v(20023.16, -76991.41) * mm});
            skLineSegment(sketch, "E326", {"start": v(18837.93, -76705.6) * mm, "end": v(18706.94, -77248.83) * mm});
            skLineSegment(sketch, "E327", {"start": v(18706.94, -77248.83) * mm, "end": v(19892.16, -77534.64) * mm});
            skSolve(sketch);
        }
        {
            var Q0;
            Q0=makeQuery(id+"F8.imprint","IMPRINT",FACE,{"disambiguationData":[TD([[makeQuery(id+"F8.imprint","IMPRINT",EDGE,{"derivedFrom":sQuery(id+"F8.wireOp",EDGE,"E27")}),1.0]])]});
            var Q1;
            {var subQ11=sQuery(id+"F8.wireOp",EDGE,"E50");Q1=makeQuery(id+"F8.imprint","IMPRINT",FACE,{"disambiguationData":[TD([[makeQuery(id+"F8.imprint","IMPRINT",EDGE,{"derivedFrom":subQ11}),-1.0]])]});}
            var Q2;
            {var subQ0=sQuery(id+"F8.wireOp",EDGE,"E65");Q2=makeQuery(id+"F8.imprint","IMPRINT",FACE,{"disambiguationData":[TD([[makeQuery(id+"F8.imprint","IMPRINT",EDGE,{"derivedFrom":subQ0}),-1.0]])]});}
            var Q3;
            {var subQ4=sQuery(id+"F8.wireOp",EDGE,"rclvcfd8-MIHF-olu5-eLjo-lo3ld7nkITQP");var subQ5=sQuery(id+"F8.wireOp",EDGE,"E61");var subQ6=makeQuery(id+"F8.imprint","INTERSECT",VERTEX,{"derivedFrom":[subQ5,subQ4]});Q3=makeQuery(id+"F8.imprint","IMPRINT",FACE,{"disambiguationData":[TD([[makeQuery(id+"F8.imprint","IMPRINT",EDGE,{"disambiguationData":[TD([[subQ6,-1.0]])],"derivedFrom":subQ5}),-1.0]])]});}
            var Q4;
            {var subQ0=sQuery(id+"F8.wireOp",EDGE,"E115");Q4=makeQuery(id+"F8.imprint","IMPRINT",FACE,{"disambiguationData":[TD([[makeQuery(id+"F8.imprint","IMPRINT",EDGE,{"derivedFrom":subQ0}),-1.0]])]});}
            var Q5;
            {var subQ0=sQuery(id+"F8.wireOp",EDGE,"PiTRZKA0-fMjo-av73-ZrMc-tVqngGcz8UUy");Q5=makeQuery(id+"F8.imprint","IMPRINT",FACE,{"disambiguationData":[TD([[makeQuery(id+"F8.imprint","IMPRINT",EDGE,{"derivedFrom":subQ0}),1.0]])]});}
            var Q6;
            {var subQ1=sQuery(id+"F8.wireOp",EDGE,"kQ18YiRS-KgXn-pTWU-JgMz-coXiSHkQz2KQ");Q6=makeQuery(id+"F8.imprint","IMPRINT",FACE,{"disambiguationData":[TD([[makeQuery(id+"F8.imprint","IMPRINT",EDGE,{"derivedFrom":subQ1}),-1.0]])]});}
            var Q7;
            {var subQ0=sQuery(id+"F8.wireOp",EDGE,"E171");Q7=makeQuery(id+"F8.imprint","IMPRINT",FACE,{"disambiguationData":[TD([[makeQuery(id+"F8.imprint","IMPRINT",EDGE,{"derivedFrom":subQ0}),-1.0]])]});}
            var Q8;
            {var subQ9=sQuery(id+"F8.wireOp",EDGE,"E112");Q8=makeQuery(id+"F8.imprint","IMPRINT",FACE,{"disambiguationData":[TD([[makeQuery(id+"F8.imprint","IMPRINT",EDGE,{"derivedFrom":subQ9}),1.0]])]});}
            var Q9;
            {var subQ5=sQuery(id+"F8.wireOp",EDGE,"GEOfW8i7-v1bV-P7JK-g7ps-RluW9onRIqib");Q9=makeQuery(id+"F8.imprint","IMPRINT",FACE,{"disambiguationData":[TD([[makeQuery(id+"F8.imprint","IMPRINT",EDGE,{"derivedFrom":subQ5}),1.0]])]});}
            var Q10;
            {var subQ0=sQuery(id+"F8.wireOp",EDGE,"E118");var subQ1=sQuery(id+"F8.wireOp",EDGE,"E113");var subQ2=makeQuery(id+"F8.imprint","INTERSECT",VERTEX,{"derivedFrom":[subQ1,subQ0]});Q10=makeQuery(id+"F8.imprint","IMPRINT",FACE,{"disambiguationData":[TD([[makeQuery(id+"F8.imprint","IMPRINT",EDGE,{"disambiguationData":[TD([[subQ2,1.0]])],"derivedFrom":subQ1}),1.0]])]});}
            var Q11;
            {var subQ0=sQuery(id+"F8.wireOp",EDGE,"E118");var subQ5=sQuery(id+"F8.wireOp",EDGE,"DJspllXv-pb2S-FSFw-zfOf-plQMQFauy2Zp");var subQ10=makeQuery(id+"F8.imprint","INTERSECT",VERTEX,{"derivedFrom":[subQ5,subQ0]});Q11=makeQuery(id+"F8.imprint","IMPRINT",FACE,{"disambiguationData":[TD([[makeQuery(id+"F8.imprint","IMPRINT",EDGE,{"disambiguationData":[TD([[subQ10,-1.0]])],"derivedFrom":subQ5}),1.0]])]});}
            var Q12;
            {var subQ0=sQuery(id+"F8.wireOp",EDGE,"E122");var subQ1=sQuery(id+"F8.wireOp",EDGE,"E119");var subQ2=makeQuery(id+"F8.imprint","INTERSECT",VERTEX,{"derivedFrom":[subQ1,subQ0]});Q12=makeQuery(id+"F8.imprint","IMPRINT",FACE,{"disambiguationData":[TD([[makeQuery(id+"F8.imprint","IMPRINT",EDGE,{"disambiguationData":[TD([[subQ2,-1.0]])],"derivedFrom":subQ1}),-1.0]])]});}
            var Q13;
            {var subQ0=sQuery(id+"F8.wireOp",EDGE,"E120");var subQ1=sQuery(id+"F8.wireOp",EDGE,"E119");var subQ2=makeQuery(id+"F8.imprint","INTERSECT",VERTEX,{"derivedFrom":[subQ1,subQ0]});Q13=makeQuery(id+"F8.imprint","IMPRINT",FACE,{"disambiguationData":[TD([[makeQuery(id+"F8.imprint","IMPRINT",EDGE,{"disambiguationData":[TD([[subQ2,1.0]])],"derivedFrom":subQ1}),-1.0]])]});}
            var Q14;
            {var subQ1=sQuery(id+"F8.wireOp",EDGE,"E67");var subQ6=sQuery(id+"F8.wireOp",EDGE,"E122");var subQ7=makeQuery(id+"F8.imprint","INTERSECT",VERTEX,{"derivedFrom":[subQ1,subQ6]});Q14=makeQuery(id+"F8.imprint","IMPRINT",FACE,{"disambiguationData":[TD([[makeQuery(id+"F8.imprint","IMPRINT",EDGE,{"disambiguationData":[TD([[subQ7,1.0]])],"derivedFrom":subQ1}),-1.0]])]});}
            var Q15;
            {var subQ4=sQuery(id+"F8.wireOp",EDGE,"E121");var subQ5=sQuery(id+"F8.wireOp",EDGE,"E67");var subQ6=makeQuery(id+"F8.imprint","INTERSECT",VERTEX,{"derivedFrom":[subQ5,subQ4]});Q15=makeQuery(id+"F8.imprint","IMPRINT",FACE,{"disambiguationData":[TD([[makeQuery(id+"F8.imprint","IMPRINT",EDGE,{"disambiguationData":[TD([[subQ6,-1.0]])],"derivedFrom":subQ4}),-1.0]])]});}
            var Q16;
            {var subQ16=sQuery(id+"F8.wireOp",EDGE,"E58.0");Q16=makeQuery(id+"F8.imprint","IMPRINT",FACE,{"disambiguationData":[TD([[makeQuery(id+"F8.imprint","IMPRINT",EDGE,{"derivedFrom":subQ16}),1.0]])]});}
            extrude(context, id + "F9", {"entities" : qUnion([Q0, Q1, Q2, Q3, Q4, Q5, Q6, Q7, Q8, Q9, Q10, Q11, Q12, Q13, Q14, Q15, Q16]), "operationType" : NewBodyOperationType.ADD, "depth" : 3048 * mm, "offsetDistance" : 25.4 * mm});
        }
    });
